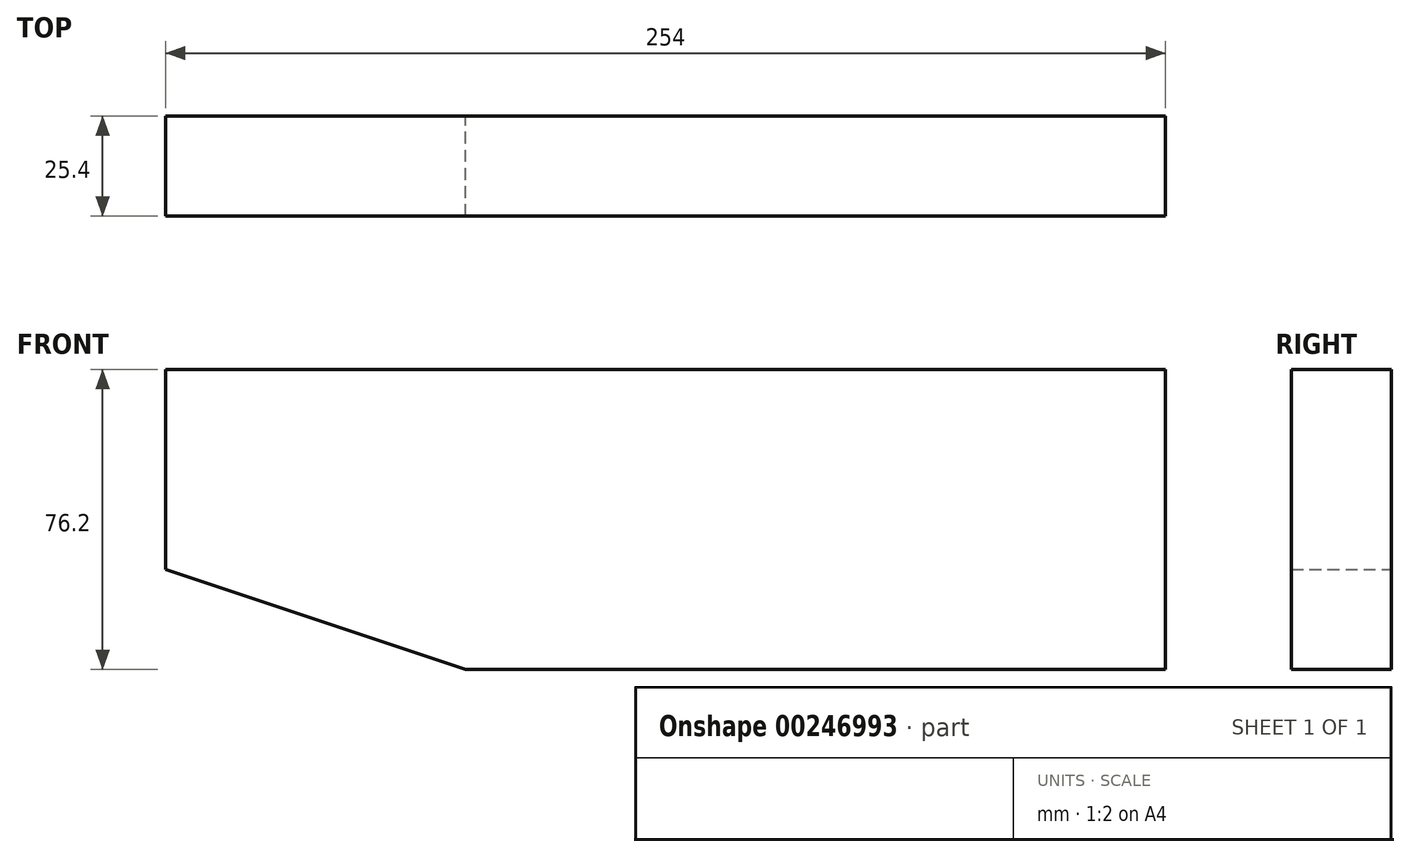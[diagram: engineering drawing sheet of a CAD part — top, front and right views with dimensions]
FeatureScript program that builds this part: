
annotation { "Feature Type Name" : "Feature", "Feature Type Description" : "" }
export const myFeature = defineFeature(function(context is Context, id is Id, definition is map)
    precondition{}
    {
        {
            var Q0;
            Q0=qCreatedBy(makeId("Front.planeOp"),FACE);
            var sketch = newSketch(context, id + "F0", { "sketchPlane" : qUnion([Q0])});
            skLineSegment(sketch, "E0", {"start": v(-62.79, 42.43) * mm, "end": v(191.21, 42.43) * mm});
            skLineSegment(sketch, "E1", {"start": v(191.21, 42.43) * mm, "end": v(191.21, -33.77) * mm});
            skLineSegment(sketch, "E2", {"start": v(191.21, -33.77) * mm, "end": v(13.41, -33.77) * mm});
            skLineSegment(sketch, "E3", {"start": v(-62.79, 42.43) * mm, "end": v(-62.79, -8.37) * mm});
            skLineSegment(sketch, "E4", {"start": v(-62.79, -8.37) * mm, "end": v(13.41, -33.77) * mm});
            skSolve(sketch);
        }
        {
            var Q0;
            Q0=makeQuery(id+"F0.imprint","IMPRINT",FACE,{"disambiguationData":[TD([[makeQuery(id+"F0.imprint","IMPRINT",EDGE,{"derivedFrom":sQuery(id+"F0.wireOp",EDGE,"E0")}),-1.0]])]});
            extrude(context, id + "F1", {"entities" : qUnion([Q0]), "depth" : 25.4 * mm});
        }
    });
